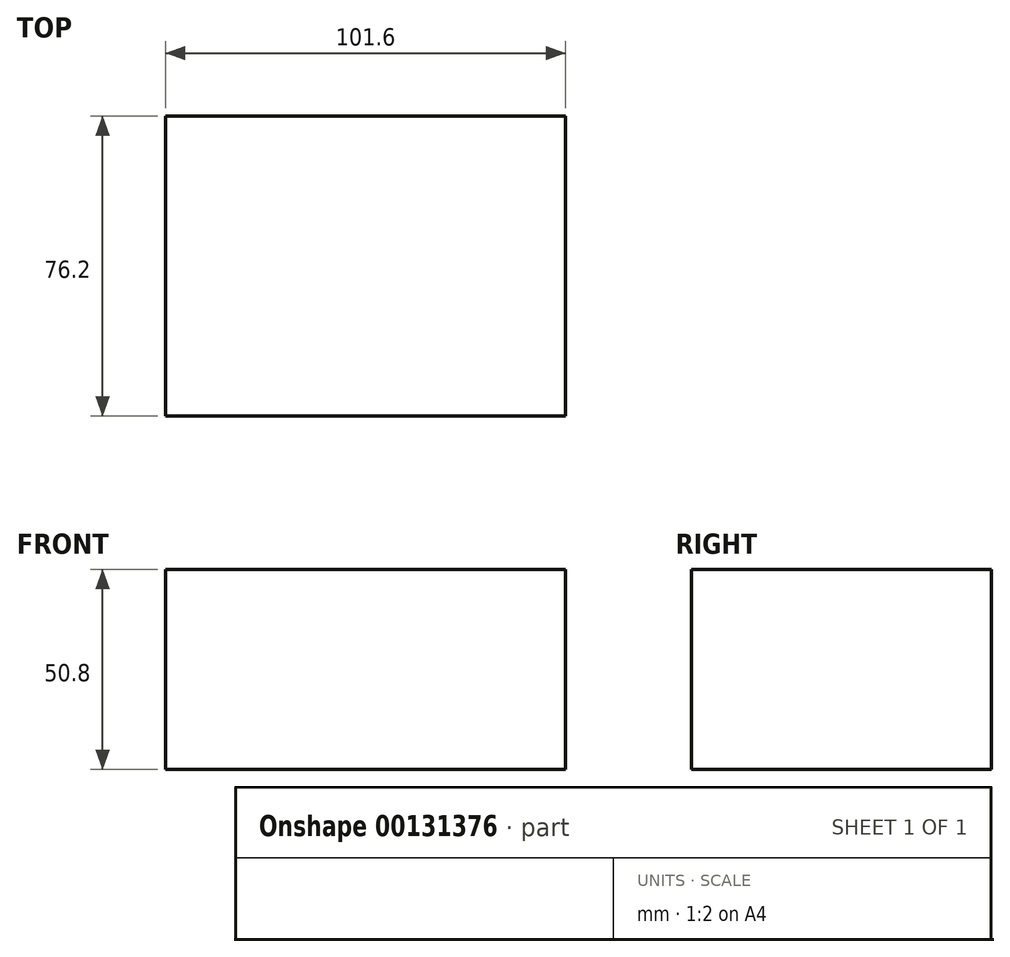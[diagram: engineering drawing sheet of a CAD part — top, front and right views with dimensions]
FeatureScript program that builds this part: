
annotation { "Feature Type Name" : "Feature", "Feature Type Description" : "" }
export const myFeature = defineFeature(function(context is Context, id is Id, definition is map)
    precondition{}
    {
        {
            var Q0;
            Q0=qCreatedBy(makeId("Front.planeOp"),FACE);
            var sketch = newSketch(context, id + "F0", { "sketchPlane" : qUnion([Q0])});
            skLineSegment(sketch, "E0.bottom", {"start": v(-62.7, 29.4) * mm, "end": v(38.9, 29.4) * mm});
            skLineSegment(sketch, "E0.top", {"start": v(-62.7, -21.4) * mm, "end": v(38.9, -21.4) * mm});
            skLineSegment(sketch, "E0.left", {"start": v(-62.7, 29.4) * mm, "end": v(-62.7, -21.4) * mm});
            skLineSegment(sketch, "E0.right", {"start": v(38.9, 29.4) * mm, "end": v(38.9, -21.4) * mm});
            skSolve(sketch);
        }
        {
            var Q0;
            Q0 = qSketchRegion(id + "F0", true);
            extrude(context, id + "F1", {"entities" : qUnion([Q0]), "depth" : 76.2 * mm});
        }
    });
